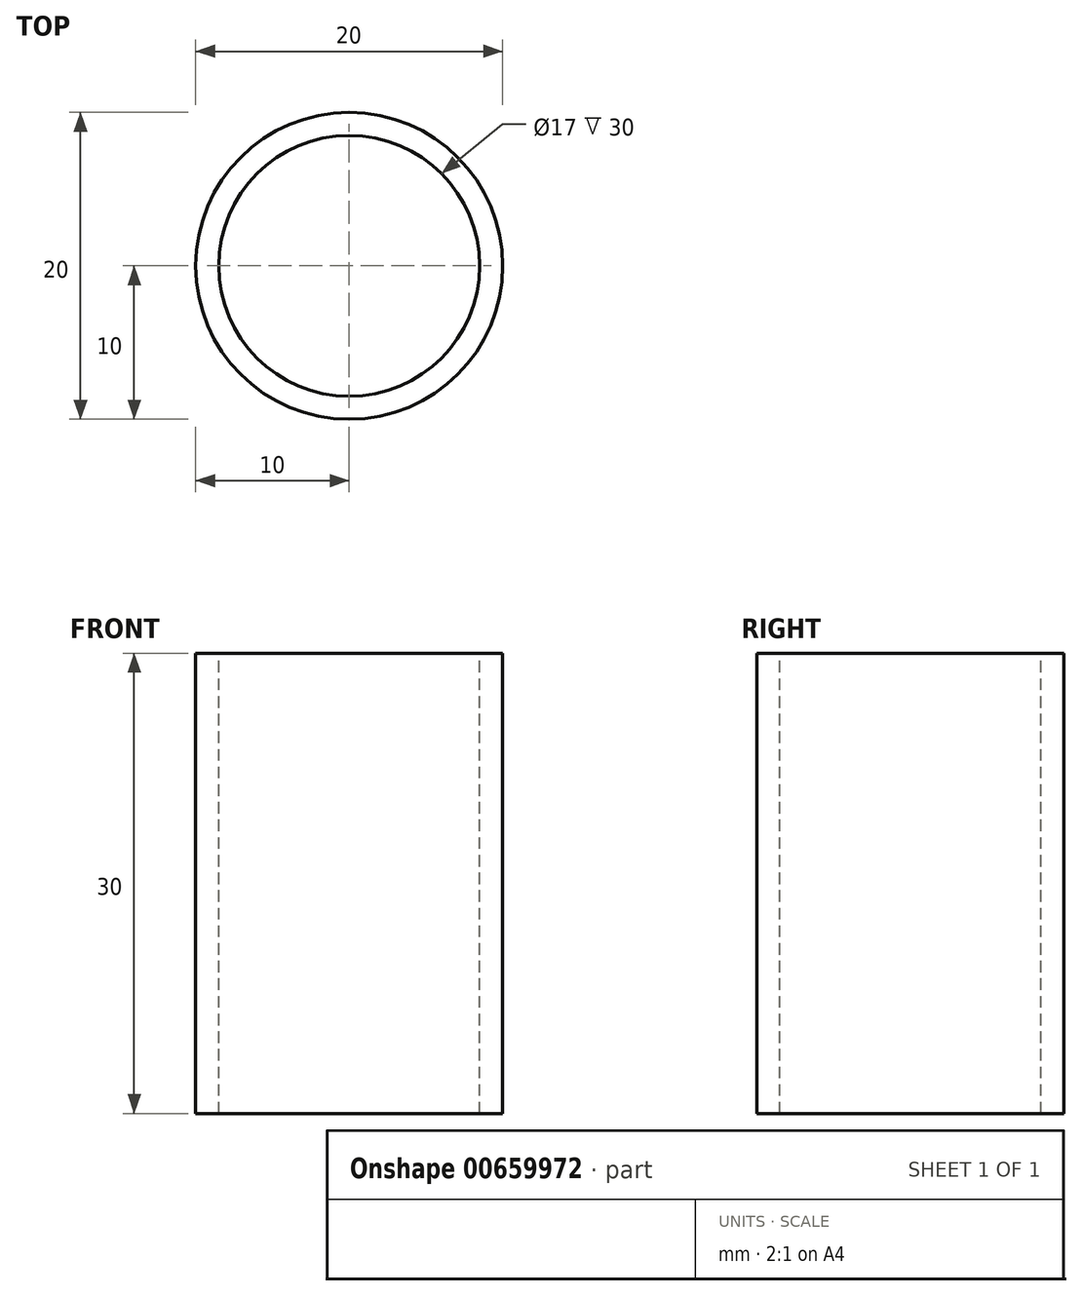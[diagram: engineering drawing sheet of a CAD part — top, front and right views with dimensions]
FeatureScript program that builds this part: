
annotation { "Feature Type Name" : "Feature", "Feature Type Description" : "" }
export const myFeature = defineFeature(function(context is Context, id is Id, definition is map)
    precondition{}
    {
        {
            var Q0;
            Q0=qCreatedBy(makeId("Top.planeOp"),FACE);
            var sketch = newSketch(context, id + "F0", { "sketchPlane" : qUnion([Q0])});
            skCircle(sketch, "E0", {"center": v(0, 0) * mm, "radius": 10 * mm});
            skCircle(sketch, "E1", {"center": v(0, 0) * mm, "radius": 8.5 * mm});
            skSolve(sketch);
        }
        {
            var Q0;
            Q0=qCreatedBy(makeId("Front.planeOp"),FACE);
            var sketch = newSketch(context, id + "F1", { "sketchPlane" : qUnion([Q0])});
            skLineSegment(sketch, "E2", {"start": v(0, 0) * mm, "end": v(0, 30) * mm});
            skSolve(sketch);
        }
        {
            var Q0;
            Q0=makeQuery(id+"F0.imprint","IMPRINT",FACE,{"disambiguationData":[TD([[makeQuery(id+"F0.imprint","IMPRINT",EDGE,{"derivedFrom":sQuery(id+"F0.wireOp",EDGE,"E0")}),1.0]])]});
            var Q1;
            Q1=sQuery(id+"F1.wireOp",EDGE,"E2");
            sweep(context, id + "F2", {"profiles" : qUnion([Q0]), "path" : qUnion([Q1])});
        }
    });
